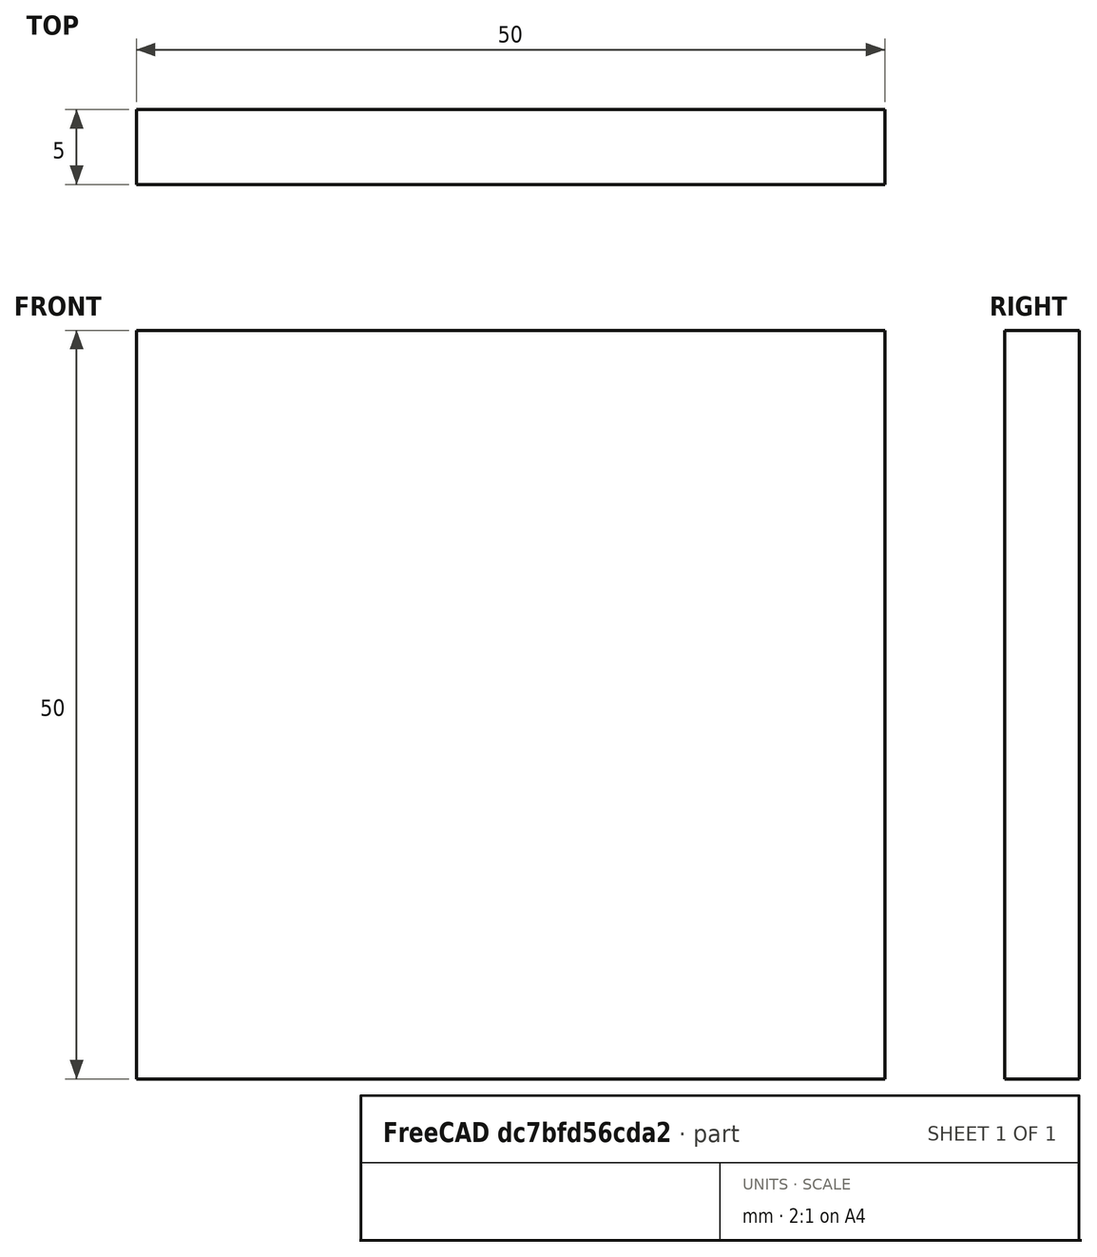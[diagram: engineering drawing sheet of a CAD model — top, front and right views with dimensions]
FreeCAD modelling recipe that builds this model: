
FCSTD DOCUMENT  (FreeCAD 0.15R4671 (Git))
Label: Flat Bar 50x5 EN10058 S235JR
License: All rights reserved
LicenseURL: http://en.wikipedia.org/wiki/All_rights_reserved
objects: Sketcher::SketchObject×1, Part::Extrusion×1
note: 2 computed .brp shape members not serialized (recipe doc carries the construction recipe); baked Part::Feature solids carry a one-line shape summary decoded from their .brp

FEATURE [Sketcher::SketchObject] Sketch
  sketch-geometry (4):
    g0: LineSegment StartX=-25 StartY=-2.5 StartZ=0 EndX=25 EndY=-2.5 EndZ=0
    g1: LineSegment StartX=25 StartY=-2.5 StartZ=0 EndX=25 EndY=2.5 EndZ=0
    g2: LineSegment StartX=25 StartY=2.5 StartZ=0 EndX=-25 EndY=2.5 EndZ=0
    g3: LineSegment StartX=-25 StartY=2.5 StartZ=0 EndX=-25 EndY=-2.5 EndZ=0
  constraints (12):
    c: Coincident(g0,g1)
    c: Coincident(g1,g2)
    c: Coincident(g2,g3)
    c: Coincident(g3,g0)
    c: Horizontal(g0)
    c: Horizontal(g2)
    c: Vertical(g1)
    c: Vertical(g3)
    c: Symmetric(g1,g2,g-2)
    c: Symmetric(g0,g1,g-1)
    c: DistanceY(g1) = 5
    c: DistanceX(g0) = 50
FEATURE [Part::Extrusion] Extrude  label="Flat Bar 50x5 EN10058 S235JR"
  Base = -> Sketch
  Dir = (0,0,50)
  Solid = true
